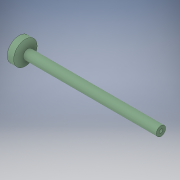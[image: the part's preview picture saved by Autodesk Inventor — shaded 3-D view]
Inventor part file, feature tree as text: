
AUTODESK INVENTOR PART (.ipt)
format: ipt  version: 2019 (Build 230136000, 136)  size: 123,392 bytes
history: native  units: mm
features: revolve x1, sketch x1
ambient origin geometry x8: Origin, YZ Plane, XZ Plane, XY Plane, X Axis, Y Axis, Z Axis, Center Point
bodies: Body1 (feature_tree)
feature tree (2):
  revolve  "Revolution2"  [1 undecoded]
  sketch  "Sketch2"  dims[d18=90.0deg]
note: 1 required parameter value undecoded (feature->parameter linkage not recoverable at this tier; creation-order binding heuristic only, values carry confidence <= 0.55)
